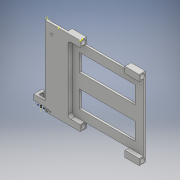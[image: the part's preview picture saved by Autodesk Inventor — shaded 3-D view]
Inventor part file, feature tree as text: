
AUTODESK INVENTOR PART (.ipt)
format: ipt  version: 2018 (Build 220112000, 112)  size: 596,992 bytes
history: native  units: mm
features: sketch x32, extrude x25, fillet x2
ambient origin geometry x8: Origin, YZ Plane, XZ Plane, XY Plane, X Axis, Y Axis, Z Axis, Center Point
bodies: Solid1 (feature_tree)
feature tree (59):
  extrude  "Extrusion1"  Depth=5.5118mm
  extrude  "Extrusion2"  Depth=8.763mm
  fillet  "Fillet1"  Radius=8.763mm
  sketch  "Sketch3"  dims[d5=5.5118mm d6=5.588mm]
  extrude  "Extrusion3"  Depth=5.5118mm
  extrude  "Extrusion4"  Depth=30.0mm TaperAngle=0.0deg
  sketch  "Sketch6"  dims[d13=3.0mm d14=18.97mm d15=0.0mm]
  extrude  "Extrusion5"  Depth=5.0mm
  extrude  "Extrusion6"  Depth=3.0mm TaperAngle=0.0deg
  sketch  "Sketch9"  dims[d21=0.0mm d22=0.0mm]
  extrude  "Extrusion7"  Depth=6.985mm
  extrude  "Extrusion8"  Depth=5.0mm TaperAngle=0.0deg
  extrude  "Extrusion9"  TaperAngle=0.0deg  [1 undecoded]
  extrude  "Extrusion10"  TaperAngle=0.0deg  [1 undecoded]
  sketch  "Sketch14"  dims[d37=3.875mm d38=6.2mm]
  sketch  "Sketch15"  dims[d39=5.0mm d40=0.0mm d41=10.0mm]
  extrude  "Extrusion11"  Depth=9.0mm
  extrude  "Extrusion12"  Depth=3.0mm TaperAngle=0.0deg
  extrude  "Extrusion13"  Depth=3.0mm TaperAngle=0.0deg
  extrude  "Extrusion14"  Depth=6.2mm
  extrude  "Extrusion15"  Depth=10.0mm
  extrude  "Extrusion16"  Depth=13.0mm TaperAngle=0.0deg
  extrude  "Extrusion17"  Depth=3.0mm TaperAngle=0.0deg
  sketch  "Sketch23"  dims[d66=30.0mm d67=0.0mm d68=100.0mm]
  extrude  "Extrusion18"  Depth=4.375mm
  extrude  "Extrusion19"  Depth=3.0mm
  extrude  "Extrusion20"  Depth=9.485mm
  sketch  "Sketch27"  dims[d78=7.75mm]
  extrude  "Extrusion21"  Depth=3.0mm
  fillet  "Fillet2"  Radius=3.0mm
  extrude  "Extrusion22"  Depth=3.0mm TaperAngle=0.0deg
  extrude  "Extrusion23"  Depth=100.0mm
  extrude  "Extrusion24"  Depth=7.75mm
  extrude  "Extrusion25"  Depth=4.0mm
  sketch  "Sketch1"  dims[d0=8.763mm d1=5.5118mm]
  sketch  "Sketch2"  dims[d2=5.588mm d3=2.3368mm d4=8.763mm]
  sketch  "Sketch4"  dims[d7=2.3368mm d8=30.0mm d9=0.0mm]
  sketch  "Sketch5"  dims[d10=0.25mm d11=0.0mm d12=5.0mm]
  sketch  "Sketch7"  dims[d16=9.485mm d17=6.985mm]
  sketch  "Sketch8"  dims[d18=3.175mm d19=5.0mm d20=0.0mm]
  sketch  "Sketch10"  dims[d23=0.0mm d26=0.0mm]
  sketch  "Sketch11"  dims[d27=0.0mm d28=9.0mm]
  sketch  "Sketch12"  dims[d29=7.75mm d30=3.0mm d31=0.0mm]
  sketch  "Sketch13"  dims[d32=4.0mm d33=8.0mm d34=3.0mm d35=0.0mm d36=0.0mm]
  sketch  "Sketch16"  dims[d42=10.0mm d43=0.0mm d44=13.0mm d45=0.0mm]
  sketch  "Sketch17"  dims[d46=3.0mm d47=8.75mm d48=0.0mm]
  sketch  "Sketch18"  dims[d49=0.0mm d52=4.375mm]
  sketch  "Sketch19"  dims[d53=4.375mm d54=3.0mm]
  sketch  "Sketch20"  dims[d55=2.0mm d56=0.0mm d57=9.485mm]
  sketch  "Sketch21"  dims[d58=6.985mm d59=6.985mm d60=3.0mm]
  sketch  "Sketch22"  dims[d61=3.0mm d62=0.0mm d63=3.0mm d64=0.0mm]
  sketch  "Sketch24"  dims[d69=12.042mm d70=7.75mm]
  sketch  "Sketch25"  dims[d71=3.0mm d72=0.0mm d73=4.0mm]
  sketch  "Sketch26"  dims[d74=9.0mm d75=3.0mm d76=0.0mm d77=0.0mm]
  sketch  "Sketch28"  dims[d79=3.875mm]
  sketch  "Sketch29"  dims[d80=3.875mm]
  sketch  "Sketch30"  dims[d81=6.2mm]
  sketch  "Sketch31"  dims[d82=4.0mm d83=0.0mm]
  sketch  "Sketch32"  dims[d84=5.512mm d85=4.375mm d86=4.375mm d87=3.0mm d88=3.0mm d89=0.0mm d90=2.0mm d91=0.0mm d92=8.763mm d93=8.763mm d94=20.25mm d95=0.0mm d96=6.5mm d97=6.5mm d98=17.25mm d99=0.0mm d100=4.0mm d101=2.75mm d102=100.0mm d103=0.0mm d104=100.0mm d105=98.425mm d106=44.45mm d107=44.45mm d108=10.0mm d109=10.0mm d110=10.0mm d111=5.0mm d112=0.0mm d113=20.0mm d114=2.75mm d115=0.0mm d116=20.0mm d117=0.0mm]
note: 2 required parameter values undecoded (feature->parameter linkage not recoverable at this tier; creation-order binding heuristic only, values carry confidence <= 0.55)
